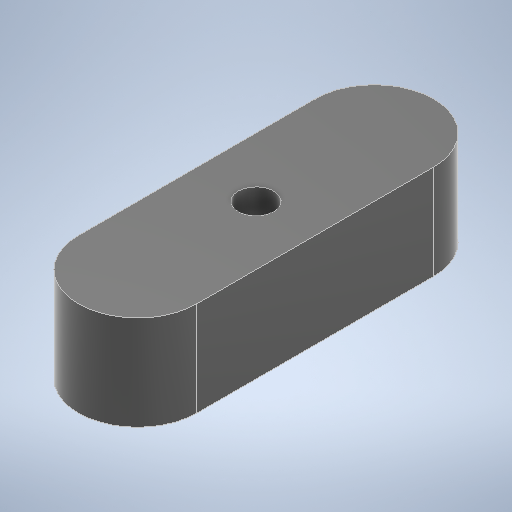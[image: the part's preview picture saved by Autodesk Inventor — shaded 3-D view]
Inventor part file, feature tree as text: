
AUTODESK INVENTOR PART (.ipt)
format: ipt  version: 2025.1 (Build 291241020, 241B)  size: 547,840 bytes
history: native  units: mm
features: sketch x2, extrude x1, hole x1, fillet x1
ambient origin geometry x8: Origin, YZ Plane, XZ Plane, XY Plane, X Axis, Y Axis, Z Axis, Center Point
bodies: Solid1 (feature_tree)
feature tree (5):
  extrude  "Extrusion1"  Depth=20.0mm
  hole  "Hole1"  [1 undecoded]
  fillet  "Fillet1"  Radius=30.0mm
  sketch  "Sketch1"  dims[d0=60.0mm d1=20.0mm]
  sketch  "Sketch2"  dims[d2=16.0mm d3=0.0mm d5=10.0mm d6=30.0mm d7=6.0mm d8=6.0mm d9=4.0mm d10=2.0mm d11=90.0deg d12=8.0mm d13=20.594885mm d14=10.0mm]
note: 1 required parameter value undecoded (feature->parameter linkage not recoverable at this tier; creation-order binding heuristic only, values carry confidence <= 0.55)
